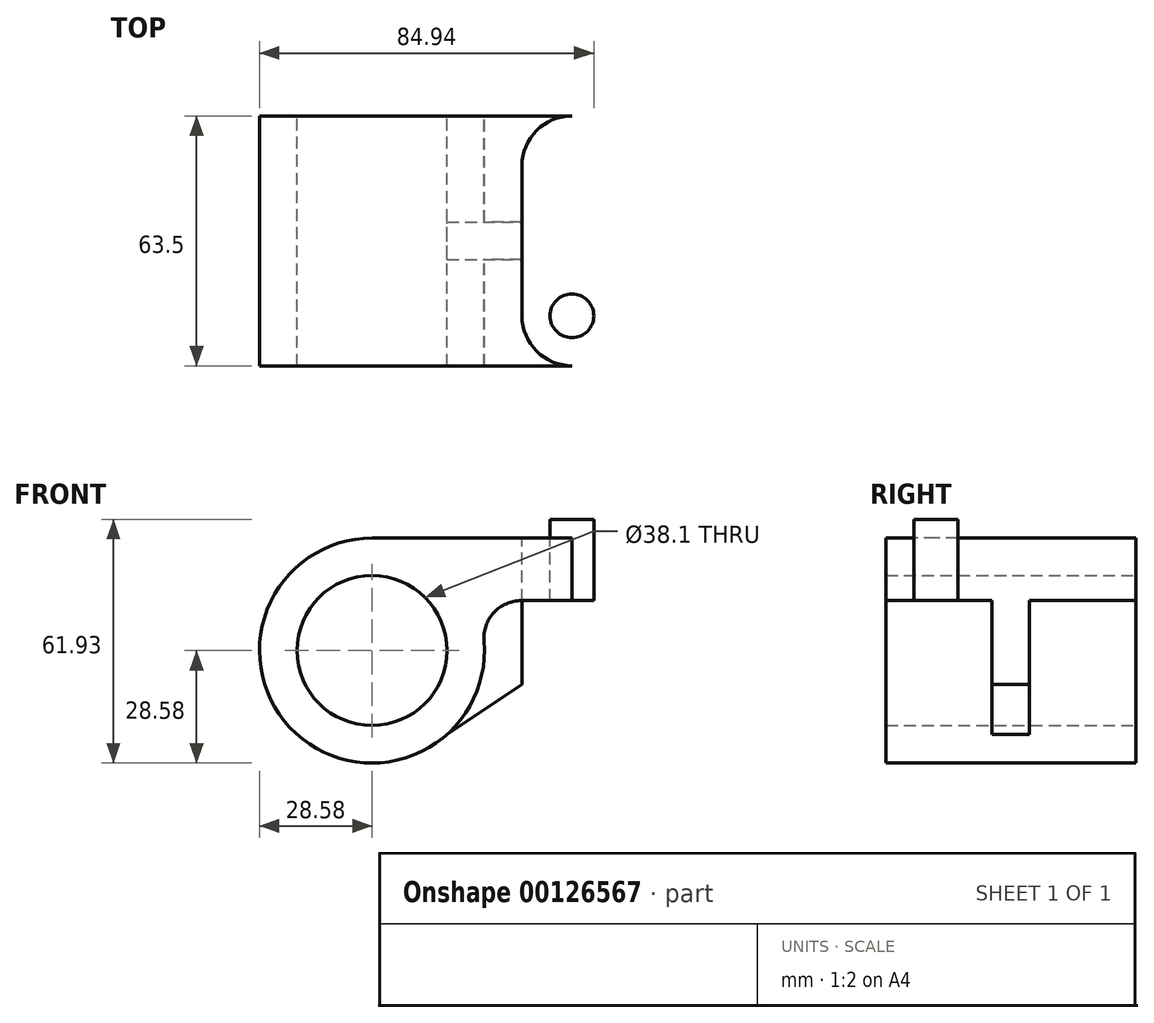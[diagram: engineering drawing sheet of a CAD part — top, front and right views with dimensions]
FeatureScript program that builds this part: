
annotation { "Feature Type Name" : "Feature", "Feature Type Description" : "" }
export const myFeature = defineFeature(function(context is Context, id is Id, definition is map)
    precondition{}
    {
        {
            var Q0;
            Q0=qCreatedBy(makeId("Front.planeOp"),FACE);
            var sketch = newSketch(context, id + "F0", { "sketchPlane" : qUnion([Q0])});
            skCircle(sketch, "E0", {"center": v(0, 0) * mm, "radius": 19.05 * mm});
            skArc(sketch, "E1.0", {"start": v(0, 28.58) * mm, "mid": v(-19.35, -21.03) * mm, "end": v(28.48, 2.38) * mm});
            skLineSegment(sketch, "E2", {"start": v(0, 28.58) * mm, "end": v(37.97, 28.58) * mm});
            skLineSegment(sketch, "E3", {"start": v(37.97, 28.58) * mm, "end": v(37.97, 33.35) * mm});
            skLineSegment(sketch, "E4", {"start": v(37.97, 33.35) * mm, "end": v(101.73, 33.35) * mm});
            skLineSegment(sketch, "E5", {"start": v(101.73, 33.35) * mm, "end": v(101.73, 12.7) * mm});
            skLineSegment(sketch, "E6", {"start": v(101.73, 12.7) * mm, "end": v(37.97, 12.7) * mm});
            skLineSegment(sketch, "E7", {"start": v(19.05, -21.3) * mm, "end": v(69.85, 12.7) * mm});
            skPoint(sketch, "E8.visualSharp", {"position": v(25.6, 12.7) * mm});
            skArc(sketch, "E8.filletArc", {"start": v(37.97, 12.7) * mm, "mid": v(30.96, 9.62) * mm, "end": v(28.48, 2.38) * mm});
            skSolve(sketch);
        }
        {
            var Q0;
            Q0=makeQuery(id+"F0.imprint","IMPRINT",FACE,{"disambiguationData":[TD([[makeQuery(id+"F0.imprint","IMPRINT",EDGE,{"derivedFrom":sQuery(id+"F0.wireOp",EDGE,"E0")}),-1.0]])]});
            extrude(context, id + "F1", {"entities" : qUnion([Q0]), "endBound" : BoundingType.SYMMETRIC, "depth" : 63.5 * mm});
        }
        {
            var Q0;
            {var subQ2=sQuery(id+"F0.wireOp",EDGE,"E7");Q0=makeQuery(id+"F0.imprint","IMPRINT",FACE,{"disambiguationData":[TD([[makeQuery(id+"F0.imprint","IMPRINT",EDGE,{"derivedFrom":subQ2}),1.0]])]});}
            extrude(context, id + "F2", {"entities" : qUnion([Q0]), "operationType" : NewBodyOperationType.ADD, "endBound" : BoundingType.SYMMETRIC, "depth" : 9.52 * mm});
        }
        {
            var Q0;
            Q0=makeQuery(id+"F1.opExtrude","SWEPT_FACE",FACE,{"disambiguationData":[OSD([sQuery(id+"F0.wireOp",EDGE,"E4")])]});
            var sketch = newSketch(context, id + "F3", { "sketchPlane" : qUnion([Q0])});
            skCircle(sketch, "E9", {"center": v(84.15, 0) * mm, "radius": 5.56 * mm});
            skCircle(sketch, "E10", {"center": v(50.8, 19.05) * mm, "radius": 5.56 * mm});
            skCircle(sketch, "E11.MirrorC", {"center": v(50.8, -19.05) * mm, "radius": 5.56 * mm});
            skArc(sketch, "E12.0", {"start": v(57.36, 29.92) * mm, "mid": v(44.56, 30.1) * mm, "end": v(38.1, 19.05) * mm});
            skArc(sketch, "E13.0", {"start": v(57.36, -29.92) * mm, "mid": v(44.56, -30.1) * mm, "end": v(38.1, -19.05) * mm});
            skArc(sketch, "E14.0", {"start": v(90.45, -11.03) * mm, "mid": v(96.85, 0) * mm, "end": v(90.45, 11.03) * mm});
            skLineSegment(sketch, "E15", {"start": v(57.36, 29.92) * mm, "end": v(90.45, 11.03) * mm});
            skLineSegment(sketch, "E16.MirrorCS", {"start": v(57.36, -29.92) * mm, "end": v(90.45, -11.03) * mm});
            skLineSegment(sketch, "E17", {"start": v(38.1, 19.05) * mm, "end": v(38.1, -19.05) * mm});
            skSolve(sketch);
        }
        {
            var Q0;
            {var subQ0=sQuery(id+"F3.wireOp",EDGE,"E17");Q0=makeQuery(id+"F3.imprint","IMPRINT",FACE,{"disambiguationData":[TD([[makeQuery(id+"F3.imprint","IMPRINT",EDGE,{"derivedFrom":subQ0}),-1.0]])]});}
            extrude(context, id + "F4", {"entities" : qUnion([Q0]), "operationType" : NewBodyOperationType.REMOVE, "oppositeDirection" : true, "depth" : 4.78 * mm});
        }
        {
            var Q0;
            Q0=makeQuery(id+"F3.imprint","IMPRINT",FACE,{"disambiguationData":[TD([[makeQuery(id+"F3.imprint","IMPRINT",EDGE,{"derivedFrom":sQuery(id+"F3.wireOp",EDGE,"E10")}),1.0]])]});
            var Q1;
            Q1=makeQuery(id+"F3.imprint","IMPRINT",FACE,{"disambiguationData":[TD([[makeQuery(id+"F3.imprint","IMPRINT",EDGE,{"derivedFrom":sQuery(id+"F3.wireOp",EDGE,"E11.MirrorC")}),-1.0]])]});
            var Q2;
            Q2=makeQuery(id+"F3.imprint","IMPRINT",FACE,{"disambiguationData":[TD([[makeQuery(id+"F3.imprint","IMPRINT",EDGE,{"derivedFrom":sQuery(id+"F3.wireOp",EDGE,"E9")}),1.0]])]});
            var Q3;
            Q3=makeQuery(id+"F3.imprint","IMPRINT",FACE,{"disambiguationData":[TD([[makeQuery(id+"F3.imprint","IMPRINT",EDGE,{"derivedFrom":sQuery(id+"F3.wireOp",EDGE,"E14.0")}),-1.0]])]});
            extrude(context, id + "F5", {"entities" : qUnion([Q0, Q1, Q2, Q3]), "operationType" : NewBodyOperationType.REMOVE, "endBound" : BoundingType.THROUGH_ALL, "oppositeDirection" : true, "depth" : 25.4 * mm});
        }
    });
